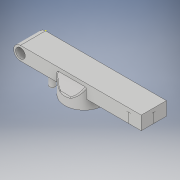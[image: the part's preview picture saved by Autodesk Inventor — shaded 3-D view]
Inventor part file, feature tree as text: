
AUTODESK INVENTOR PART (.ipt)
format: ipt  version: 2019 (Build 230136000, 136)  size: 230,912 bytes
history: native  units: in
note: dims shown in document units (in); Inventor stores cm internally (conversion verified against a paired STEP export)
features: sketch x6, extrude x4, fillet x3, chamfer x2
ambient origin geometry x8: Origin, YZ Plane, XZ Plane, XY Plane, X Axis, Y Axis, Z Axis, Center Point
bodies: Solid1 (feature_tree)
feature tree (15):
  extrude  "Extrusion1"  Depth=2.4606in
  extrude  "Extrusion2"  Depth=0.5118in TaperAngle=0.0deg
  extrude  "Extrusion3"  Depth=0.1969in TaperAngle=0.0deg
  sketch  "Sketch4"  dims[d9=2.2047in]
  chamfer  "Chamfer1"  Distance=0.1969in
  chamfer  "Chamfer2"  Distance=0.2559in
  extrude  "Extrusion4"  Depth=0.1181in TaperAngle=120.0deg
  fillet  "Fillet1"  Radius=0.1181in
  fillet  "Fillet2"  Radius=0.1181in
  fillet  "Fillet3"  Radius=0.3937in
  sketch  "Sketch6"  dims[d15=0.2559in d16=0.2559in d17=0.1181in d18=0.0787in d19=120.0deg d20=0.1181in d21=0.0787in d22=120.0deg d23=0.1181in d24=0.3937in d25=0.3937in d26=0.0in d27=0.0394in d28=0.0394in d29=0.0394in d30=1.1811in]
  sketch  "Sketch1"  dims[d0=0.1969in d2=2.4606in]
  sketch  "Sketch2"  dims[d3=0.1378in d4=0.5118in d5=0.0in]
  sketch  "Sketch3"  dims[d6=0.5118in d7=0.1969in d8=0.0in]
  sketch  "Sketch5"  dims[d11=0.7874in d13=0.1969in d14=0.0in]
